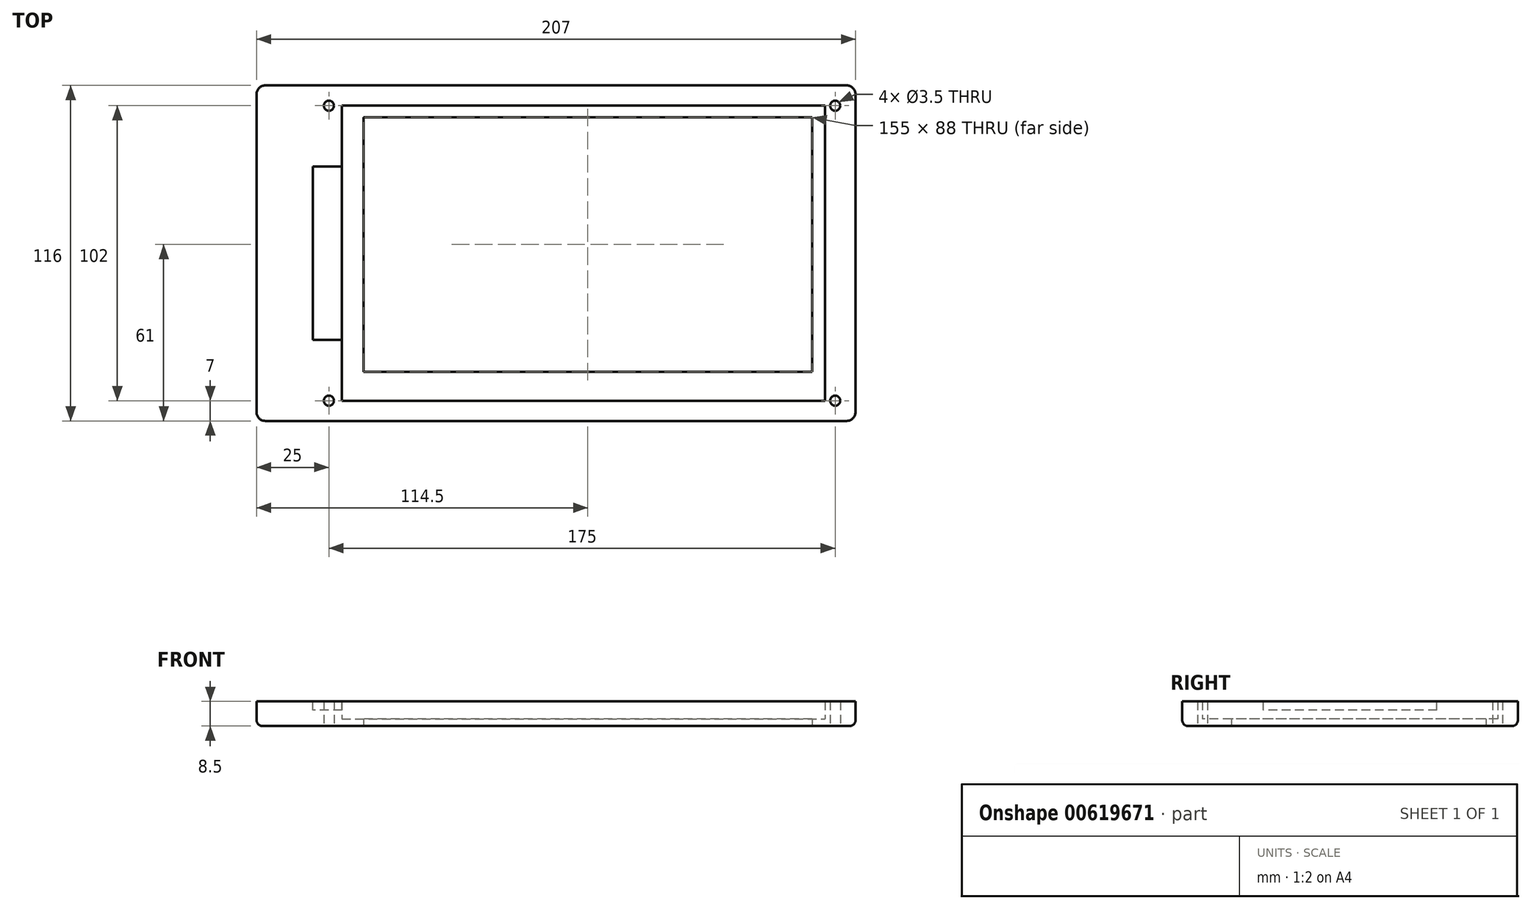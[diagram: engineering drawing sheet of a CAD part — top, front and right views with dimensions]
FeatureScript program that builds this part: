
annotation { "Feature Type Name" : "Feature", "Feature Type Description" : "" }
export const myFeature = defineFeature(function(context is Context, id is Id, definition is map)
    precondition{}
    {
        {
            var Q0;
            Q0=qCreatedBy(makeId("Top.planeOp"),FACE);
            var sketch = newSketch(context, id + "F0", { "sketchPlane" : qUnion([Q0])});
            skLineSegment(sketch, "E0.bottom", {"start": v(0, 0) * mm, "end": v(207, 0) * mm});
            skLineSegment(sketch, "E0.top", {"start": v(0, -116) * mm, "end": v(207, -116) * mm});
            skLineSegment(sketch, "E0.left", {"start": v(0, 0) * mm, "end": v(0, -116) * mm});
            skLineSegment(sketch, "E0.right", {"start": v(207, 0) * mm, "end": v(207, -116) * mm});
            skSolve(sketch);
        }
        {
            var Q0;
            Q0=makeQuery(id+"F0.imprint","IMPRINT",FACE,{"disambiguationData":[TD([[makeQuery(id+"F0.imprint","IMPRINT",EDGE,{"derivedFrom":sQuery(id+"F0.wireOp",EDGE,"E0.bottom")}),-1.0]])]});
            extrude(context, id + "F1", {"entities" : qUnion([Q0]), "depth" : 6 * mm, "offsetDistance" : 25 * mm});
        }
        {
            var Q0;
            Q0=makeQuery(id+"F0.imprint","IMPRINT",FACE,{"disambiguationData":[TD([[makeQuery(id+"F0.imprint","IMPRINT",EDGE,{"derivedFrom":sQuery(id+"F0.wireOp",EDGE,"E0.bottom")}),-1.0]])]});
            var sketch = newSketch(context, id + "F2", { "sketchPlane" : qUnion([Q0])});
            skLineSegment(sketch, "E1.bottom", {"start": v(29.5, -7) * mm, "end": v(196.5, -7) * mm});
            skLineSegment(sketch, "E1.top", {"start": v(29.5, -109) * mm, "end": v(196.5, -109) * mm});
            skLineSegment(sketch, "E1.left", {"start": v(29.5, -7) * mm, "end": v(29.5, -109) * mm});
            skLineSegment(sketch, "E1.right", {"start": v(196.5, -7) * mm, "end": v(196.5, -109) * mm});
            skSolve(sketch);
        }
        {
            var Q0;
            Q0=makeQuery(id+"F2.imprint","IMPRINT",FACE,{"disambiguationData":[TD([[makeQuery(id+"F2.imprint","IMPRINT",EDGE,{"derivedFrom":sQuery(id+"F2.wireOp",EDGE,"E1.bottom")}),-1.0]])]});
            extrude(context, id + "F3", {"entities" : qUnion([Q0]), "operationType" : NewBodyOperationType.REMOVE, "depth" : 6 * mm, "offsetDistance" : 25 * mm});
        }
        {
            var Q0;
            Q0=makeQuery(id+"F1.opExtrude","CAP_FACE",FACE,{"disambiguationData":[OSD([sQuery(id+"F0.wireOp",EDGE,"E0.bottom"),sQuery(id+"F0.wireOp",EDGE,"E0.top"),sQuery(id+"F0.wireOp",EDGE,"E0.left"),sQuery(id+"F0.wireOp",EDGE,"E0.right")])],"isStart":true});
            var sketch = newSketch(context, id + "F4", { "sketchPlane" : qUnion([Q0])});
            skLineSegment(sketch, "E2", {"start": v(207, 7) * mm, "end": v(0, 7) * mm, "construction": true});
            skCircle(sketch, "E3", {"center": v(200, 7) * mm, "radius": 1.75 * mm});
            skCircle(sketch, "E4", {"center": v(25, 7) * mm, "radius": 1.75 * mm});
            skLineSegment(sketch, "E5", {"start": v(207, 109) * mm, "end": v(0, 109) * mm, "construction": true});
            skCircle(sketch, "E6", {"center": v(200, 109) * mm, "radius": 1.75 * mm});
            skCircle(sketch, "E7", {"center": v(25, 109) * mm, "radius": 1.75 * mm});
            skSolve(sketch);
        }
        {
            var Q0;
            Q0=makeQuery(id+"F4.imprint","IMPRINT",FACE,{"disambiguationData":[TD([[makeQuery(id+"F4.imprint","IMPRINT",EDGE,{"derivedFrom":sQuery(id+"F4.wireOp",EDGE,"E3")}),1.0]])]});
            var Q1;
            Q1=makeQuery(id+"F4.imprint","IMPRINT",FACE,{"disambiguationData":[TD([[makeQuery(id+"F4.imprint","IMPRINT",EDGE,{"derivedFrom":sQuery(id+"F4.wireOp",EDGE,"E6")}),1.0]])]});
            var Q2;
            Q2=makeQuery(id+"F4.imprint","IMPRINT",FACE,{"disambiguationData":[TD([[makeQuery(id+"F4.imprint","IMPRINT",EDGE,{"derivedFrom":sQuery(id+"F4.wireOp",EDGE,"E7")}),1.0]])]});
            var Q3;
            Q3=makeQuery(id+"F4.imprint","IMPRINT",FACE,{"disambiguationData":[TD([[makeQuery(id+"F4.imprint","IMPRINT",EDGE,{"derivedFrom":sQuery(id+"F4.wireOp",EDGE,"E4")}),1.0]])]});
            extrude(context, id + "F5", {"entities" : qUnion([Q0, Q1, Q2, Q3]), "operationType" : NewBodyOperationType.REMOVE, "oppositeDirection" : true, "depth" : 25 * mm, "offsetDistance" : 25 * mm});
        }
        {
            var Q0;
            Q0=makeQuery(id+"F1.opExtrude","CAP_FACE",FACE,{"disambiguationData":[OSD([sQuery(id+"F0.wireOp",EDGE,"E0.bottom"),sQuery(id+"F0.wireOp",EDGE,"E0.top"),sQuery(id+"F0.wireOp",EDGE,"E0.left"),sQuery(id+"F0.wireOp",EDGE,"E0.right")])],"isStart":false});
            var sketch = newSketch(context, id + "F6", { "sketchPlane" : qUnion([Q0])});
            skLineSegment(sketch, "E8.bottom", {"start": v(29.5, -28) * mm, "end": v(19.5, -28) * mm});
            skLineSegment(sketch, "E8.top", {"start": v(29.5, -88) * mm, "end": v(19.5, -88) * mm});
            skLineSegment(sketch, "E8.left", {"start": v(29.5, -28) * mm, "end": v(29.5, -88) * mm});
            skLineSegment(sketch, "E8.right", {"start": v(19.5, -28) * mm, "end": v(19.5, -88) * mm});
            skSolve(sketch);
        }
        {
            var Q0;
            Q0=makeQuery(id+"F6.imprint","IMPRINT",FACE,{"disambiguationData":[TD([[makeQuery(id+"F6.imprint","IMPRINT",EDGE,{"derivedFrom":sQuery(id+"F6.wireOp",EDGE,"E8.bottom")}),1.0]])]});
            extrude(context, id + "F7", {"entities" : qUnion([Q0]), "operationType" : NewBodyOperationType.REMOVE, "oppositeDirection" : true, "depth" : 3 * mm, "offsetDistance" : 25 * mm});
        }
        {
            var Q0;
            Q0=makeQuery(id+"F1.opExtrude","CAP_FACE",FACE,{"disambiguationData":[OSD([sQuery(id+"F0.wireOp",EDGE,"E0.bottom"),sQuery(id+"F0.wireOp",EDGE,"E0.top"),sQuery(id+"F0.wireOp",EDGE,"E0.left"),sQuery(id+"F0.wireOp",EDGE,"E0.right")])],"isStart":true});
            var sketch = newSketch(context, id + "F8", { "sketchPlane" : qUnion([Q0])});
            skLineSegment(sketch, "E9.bottom", {"start": v(207, 0) * mm, "end": v(0, 0) * mm});
            skLineSegment(sketch, "E9.top", {"start": v(207, 116) * mm, "end": v(0, 116) * mm});
            skLineSegment(sketch, "E9.left", {"start": v(207, 0) * mm, "end": v(207, 116) * mm});
            skLineSegment(sketch, "E9.right", {"start": v(0, 0) * mm, "end": v(0, 116) * mm});
            skLineSegment(sketch, "E10.bottom", {"start": v(196.5, 7) * mm, "end": v(29.5, 7) * mm});
            skLineSegment(sketch, "E10.top", {"start": v(196.5, 109) * mm, "end": v(29.5, 109) * mm});
            skLineSegment(sketch, "E10.left", {"start": v(196.5, 7) * mm, "end": v(196.5, 109) * mm});
            skLineSegment(sketch, "E10.right", {"start": v(29.5, 7) * mm, "end": v(29.5, 109) * mm});
            skSolve(sketch);
        }
        {
            var Q0;
            Q0=makeQuery(id+"F8.imprint","IMPRINT",FACE,{"disambiguationData":[TD([[makeQuery(id+"F8.imprint","IMPRINT",EDGE,{"derivedFrom":sQuery(id+"F8.wireOp",EDGE,"E10.bottom")}),1.0]])]});
            var Q1;
            Q1=makeQuery(id+"F8.imprint","IMPRINT",FACE,{"disambiguationData":[TD([[makeQuery(id+"F8.imprint","IMPRINT",EDGE,{"derivedFrom":sQuery(id+"F8.wireOp",EDGE,"E9.bottom")}),1.0]])]});
            extrude(context, id + "F9", {"entities" : qUnion([Q0, Q1]), "operationType" : NewBodyOperationType.ADD, "depth" : 2.5 * mm, "offsetDistance" : 25 * mm});
        }
        {
            var Q0;
            Q0=makeQuery(id+"F9.opExtrude","CAP_FACE",FACE,{"disambiguationData":[OSD([sQuery(id+"F4.wireOp",EDGE,"E3"),sQuery(id+"F4.wireOp",EDGE,"E4"),sQuery(id+"F4.wireOp",EDGE,"E6"),sQuery(id+"F4.wireOp",EDGE,"E7"),sQuery(id+"F8.wireOp",EDGE,"E9.bottom"),sQuery(id+"F8.wireOp",EDGE,"E9.top"),sQuery(id+"F8.wireOp",EDGE,"E9.left"),sQuery(id+"F8.wireOp",EDGE,"E9.right")])],"isStart":false});
            var sketch = newSketch(context, id + "F10", { "sketchPlane" : qUnion([Q0])});
            skLineSegment(sketch, "E11.bottom", {"start": v(192, 11) * mm, "end": v(37, 11) * mm});
            skLineSegment(sketch, "E11.top", {"start": v(192, 99) * mm, "end": v(37, 99) * mm});
            skLineSegment(sketch, "E11.left", {"start": v(192, 11) * mm, "end": v(192, 99) * mm});
            skLineSegment(sketch, "E11.right", {"start": v(37, 11) * mm, "end": v(37, 99) * mm});
            skSolve(sketch);
        }
        {
            var Q0;
            Q0=makeQuery(id+"F10.imprint","IMPRINT",FACE,{"disambiguationData":[TD([[makeQuery(id+"F10.imprint","IMPRINT",EDGE,{"derivedFrom":sQuery(id+"F10.wireOp",EDGE,"E11.bottom")}),-1.0]])]});
            extrude(context, id + "F11", {"entities" : qUnion([Q0]), "operationType" : NewBodyOperationType.REMOVE, "oppositeDirection" : true, "depth" : 25 * mm, "offsetDistance" : 25 * mm});
        }
        {
            var Q0;
            Q0=makeQuery(id+"Fak5G2CP7K3yYCP_1.opThicken","CAP_FACE",FACE,{"disambiguationData":[OSD([sQuery(id+"F0.wireOp",EDGE,"E0.bottom"),sQuery(id+"F0.wireOp",EDGE,"E0.top"),sQuery(id+"F0.wireOp",EDGE,"E0.left"),sQuery(id+"F0.wireOp",EDGE,"E0.right")])],"isStart":true});
            var sketch = newSketch(context, id + "F12", { "sketchPlane" : qUnion([Q0])});
            skLineSegment(sketch, "E12.bottom", {"start": v(204.5, -53) * mm, "end": v(207, -53) * mm});
            skLineSegment(sketch, "E12.top", {"start": v(204.5, -116) * mm, "end": v(207, -116) * mm});
            skLineSegment(sketch, "E12.left", {"start": v(204.5, -53) * mm, "end": v(204.5, -116) * mm});
            skLineSegment(sketch, "E12.right", {"start": v(207, -53) * mm, "end": v(207, -116) * mm});
            skSolve(sketch);
        }
        {
            var Q0;
            {var subQ0=sQuery(id+"F0.wireOp",EDGE,"E0.right");var subQ1=sQuery(id+"F0.wireOp",EDGE,"E0.bottom");Q0=makeQuery(id+"F9.boolean.opBoolean","MERGE",EDGE,{"derivedFrom":[makeQuery(id+"Fak5G2CP7K3yYCP_1.boolean.opBoolean","MERGE",EDGE,{"derivedFrom":[makeQuery(id+"F1.opExtrude","SWEPT_EDGE",EDGE,{"disambiguationData":[OSD([subQ1,subQ0])]}),makeQuery(id+"Fak5G2CP7K3yYCP_1.opThicken","SWEPT_EDGE",EDGE,{"disambiguationData":[OSD([subQ1,subQ0])]})]}),makeQuery(id+"F9.opExtrude","SWEPT_EDGE",EDGE,{"disambiguationData":[OSD([sQuery(id+"F8.wireOp",EDGE,"E9.bottom"),sQuery(id+"F8.wireOp",EDGE,"E9.left")])]})]});}
            var Q1;
            {var subQ0=sQuery(id+"F0.wireOp",EDGE,"E0.right");var subQ1=sQuery(id+"F0.wireOp",EDGE,"E0.top");Q1=makeQuery(id+"FbFTSfMYaCfkktB_1.boolean.opBoolean","MERGE",EDGE,{"derivedFrom":[makeQuery(id+"F9.boolean.opBoolean","MERGE",EDGE,{"derivedFrom":[makeQuery(id+"Fak5G2CP7K3yYCP_1.boolean.opBoolean","MERGE",EDGE,{"derivedFrom":[makeQuery(id+"F1.opExtrude","SWEPT_EDGE",EDGE,{"disambiguationData":[OSD([subQ1,subQ0])]}),makeQuery(id+"Fak5G2CP7K3yYCP_1.opThicken","SWEPT_EDGE",EDGE,{"disambiguationData":[OSD([subQ1,subQ0])]})]}),makeQuery(id+"F9.opExtrude","SWEPT_EDGE",EDGE,{"disambiguationData":[OSD([sQuery(id+"F8.wireOp",EDGE,"E9.top"),sQuery(id+"F8.wireOp",EDGE,"E9.left")])]})]}),makeQuery(id+"FbFTSfMYaCfkktB_1.opExtrude","SWEPT_EDGE",EDGE,{"disambiguationData":[OSD([sQuery(id+"F12.wireOp",EDGE,"E12.top"),sQuery(id+"F12.wireOp",EDGE,"E12.right")])]})]});}
            var Q2;
            {var subQ0=sQuery(id+"F0.wireOp",EDGE,"E0.left");var subQ1=sQuery(id+"F0.wireOp",EDGE,"E0.top");Q2=makeQuery(id+"FbFTSfMYaCfkktB_1.boolean.opBoolean","MERGE",EDGE,{"derivedFrom":[makeQuery(id+"F9.boolean.opBoolean","MERGE",EDGE,{"derivedFrom":[makeQuery(id+"Fak5G2CP7K3yYCP_1.boolean.opBoolean","MERGE",EDGE,{"derivedFrom":[makeQuery(id+"F1.opExtrude","SWEPT_EDGE",EDGE,{"disambiguationData":[OSD([subQ1,subQ0])]}),makeQuery(id+"Fak5G2CP7K3yYCP_1.opThicken","SWEPT_EDGE",EDGE,{"disambiguationData":[OSD([subQ1,subQ0])]})]}),makeQuery(id+"F9.opExtrude","SWEPT_EDGE",EDGE,{"disambiguationData":[OSD([sQuery(id+"F8.wireOp",EDGE,"E9.top"),sQuery(id+"F8.wireOp",EDGE,"E9.right")])]})]}),makeQuery(id+"FbFTSfMYaCfkktB_1.opExtrude","SWEPT_EDGE",EDGE,{"disambiguationData":[OSD([sQuery(id+"FiOIHTl7Iq9vGq3_1.wireOp",EDGE,"PMrV09hO-P6FE-FF9L-VazH-uKaAR14bYIPV.top"),sQuery(id+"FiOIHTl7Iq9vGq3_1.wireOp",EDGE,"PMrV09hO-P6FE-FF9L-VazH-uKaAR14bYIPV.left")])]})]});}
            var Q3;
            {var subQ0=sQuery(id+"F0.wireOp",EDGE,"E0.left");var subQ1=sQuery(id+"F0.wireOp",EDGE,"E0.bottom");Q3=makeQuery(id+"F9.boolean.opBoolean","MERGE",EDGE,{"derivedFrom":[makeQuery(id+"Fak5G2CP7K3yYCP_1.boolean.opBoolean","MERGE",EDGE,{"derivedFrom":[makeQuery(id+"F1.opExtrude","SWEPT_EDGE",EDGE,{"disambiguationData":[OSD([subQ1,subQ0])]}),makeQuery(id+"Fak5G2CP7K3yYCP_1.opThicken","SWEPT_EDGE",EDGE,{"disambiguationData":[OSD([subQ1,subQ0])]})]}),makeQuery(id+"F9.opExtrude","SWEPT_EDGE",EDGE,{"disambiguationData":[OSD([sQuery(id+"F8.wireOp",EDGE,"E9.bottom"),sQuery(id+"F8.wireOp",EDGE,"E9.right")])]})]});}
            fillet(context, id + "F13", {"entities" : qUnion([Q0, Q1, Q2, Q3]), "radius" : 3 * mm, "tangentPropagation" : true, "allowEdgeOverflow" : false});
        }
        {
            var Q0;
            Q0=makeQuery(id+"F9.opExtrude","CAP_EDGE",EDGE,{"disambiguationData":[OSD([sQuery(id+"F8.wireOp",EDGE,"E9.right")])],"isStart":false});
            var Q1;
            Q1=makeQuery(id+"F11.boolean.opBoolean","COPY",EDGE,{"derivedFrom":makeQuery(id+"F11.opExtrude","CAP_EDGE",EDGE,{"disambiguationData":[OSD([sQuery(id+"F10.wireOp",EDGE,"E11.top")])],"isStart":true})});
            var Q2;
            Q2=makeQuery(id+"F11.boolean.opBoolean","COPY",EDGE,{"derivedFrom":makeQuery(id+"F11.opExtrude","CAP_EDGE",EDGE,{"disambiguationData":[OSD([sQuery(id+"F10.wireOp",EDGE,"E11.right")])],"isStart":true})});
            var Q3;
            Q3=makeQuery(id+"F11.boolean.opBoolean","COPY",EDGE,{"derivedFrom":makeQuery(id+"F11.opExtrude","CAP_EDGE",EDGE,{"disambiguationData":[OSD([sQuery(id+"F10.wireOp",EDGE,"E11.left")])],"isStart":true})});
            var Q4;
            Q4=makeQuery(id+"F11.boolean.opBoolean","COPY",EDGE,{"derivedFrom":makeQuery(id+"F11.opExtrude","CAP_EDGE",EDGE,{"disambiguationData":[OSD([sQuery(id+"F10.wireOp",EDGE,"E11.bottom")])],"isStart":true})});
            fillet(context, id + "F14", {"entities" : qUnion([Q0, Q1, Q2, Q3, Q4]), "radius" : 2 * mm, "tangentPropagation" : true, "allowEdgeOverflow" : false});
        }
    });
